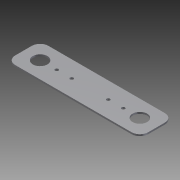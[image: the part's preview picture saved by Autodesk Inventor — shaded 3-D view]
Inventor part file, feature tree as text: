
AUTODESK INVENTOR PART (.ipt)
format: ipt  version: 2012 (Build 160160000, 160)  size: 97,792 bytes
history: native  units: mm
features: extrude x1, sketch x1
ambient origin geometry x8: Origin, YZ Plane, XZ Plane, XY Plane, X Axis, Y Axis, Z Axis, Center Point
bodies: Solid1 (feature_tree)
feature tree (2):
  extrude  "Extrusion1"  Depth=1.0mm TaperAngle=0.0deg
  sketch  "Sketch1"  dims[d109=10.0mm d110=10.0mm d111=8.77mm d112=8.77mm d113=2.0mm d114=2.0mm d115=10.0mm d116=9.0mm d117=2.0mm d118=2.0mm d119=10.0mm d120=9.0mm d121=60.0mm d126=10.0mm d399=1.0mm d400=0.0mm d401=20.0mm]
